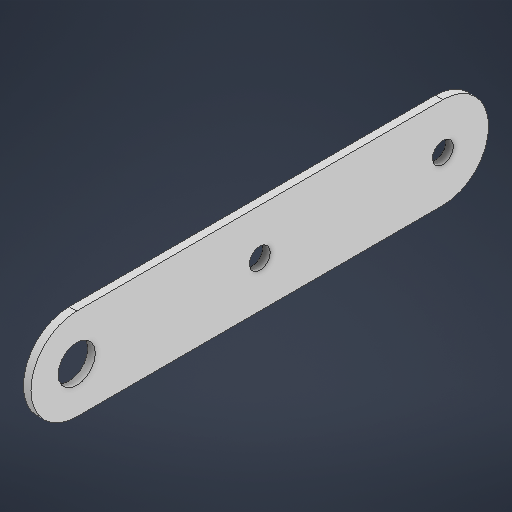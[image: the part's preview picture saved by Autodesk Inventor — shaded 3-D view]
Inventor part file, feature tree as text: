
AUTODESK INVENTOR PART (.ipt)
format: ipt  version: 2025.2 (Build 292293000, 293)  size: 188,416 bytes
history: native  units: in
note: dims shown in document units (in); Inventor stores cm internally (conversion verified against a paired STEP export)
features: extrude x1, sketch x1
ambient origin geometry x8: Origin, YZ Plane, XZ Plane, XY Plane, X Axis, Y Axis, Z Axis, Center Point
bodies: Solid1 (feature_tree)
feature tree (2):
  extrude  "Extrusion1"  Depth=0.75in
  sketch  "Sketch1"  dims[d0=0.305in d1=0.75in d2=0.172in d3=3.0in d4=0.75in d6=0.0625in d7=0.0in d9=0.172in]
